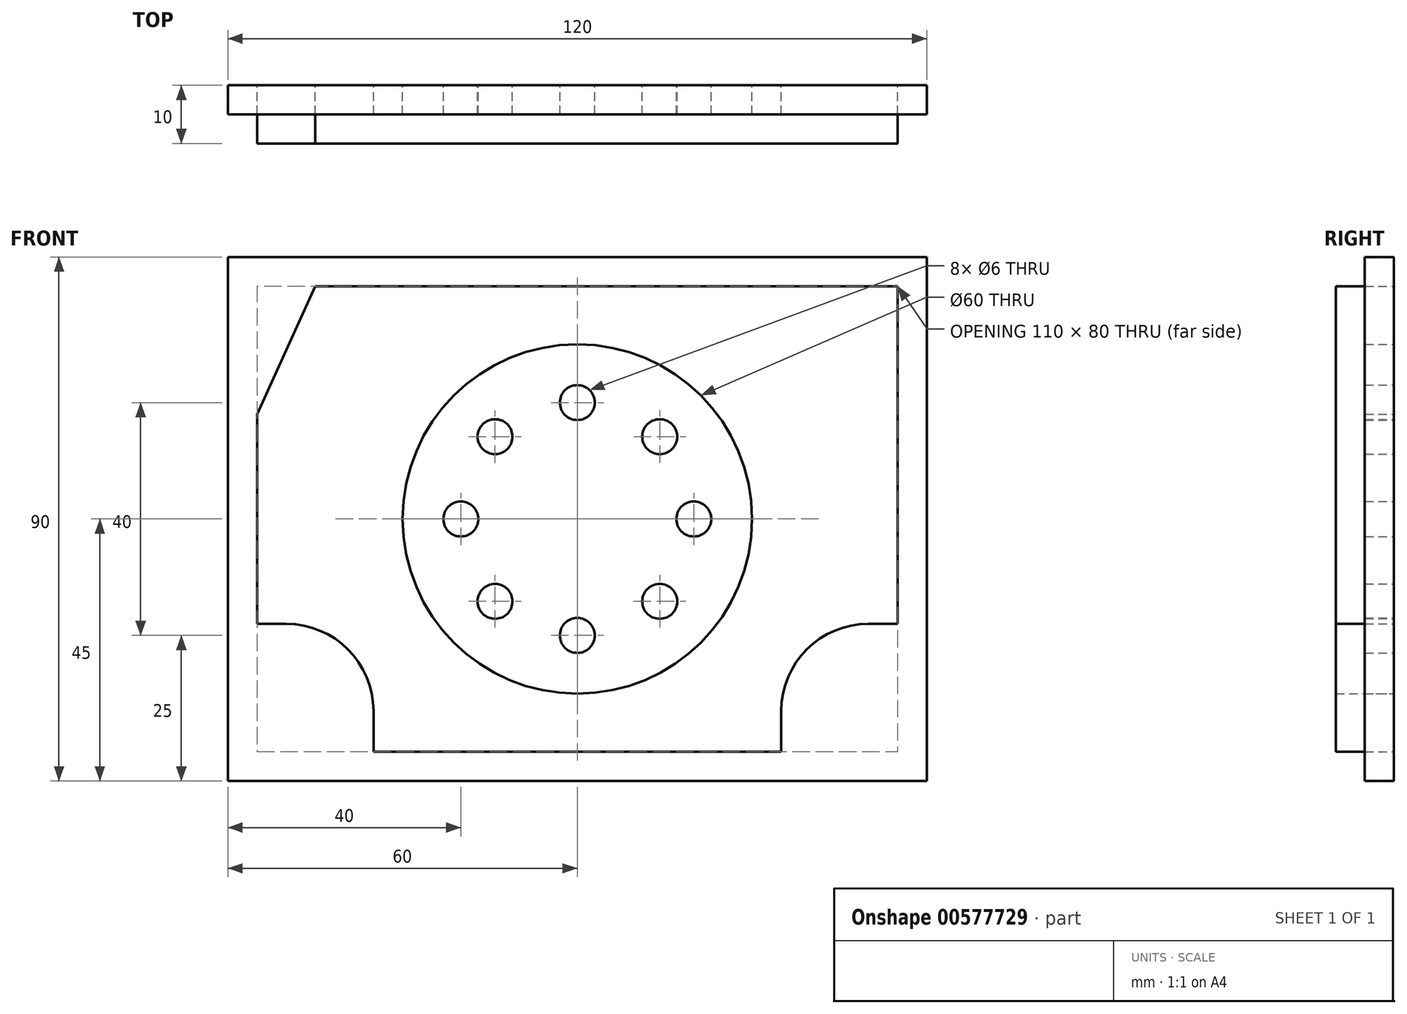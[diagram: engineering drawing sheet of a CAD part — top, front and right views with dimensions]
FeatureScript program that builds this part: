
annotation { "Feature Type Name" : "Feature", "Feature Type Description" : "" }
export const myFeature = defineFeature(function(context is Context, id is Id, definition is map)
    precondition{}
    {
        {
            var Q0;
            Q0=qCreatedBy(makeId("Front.planeOp"),FACE);
            var sketch = newSketch(context, id + "F0", { "sketchPlane" : qUnion([Q0])});
            skLineSegment(sketch, "E0", {"start": v(0, 0) * mm, "end": v(-120, 0) * mm});
            skLineSegment(sketch, "E1", {"start": v(-120, 0) * mm, "end": v(-120, 90) * mm});
            skLineSegment(sketch, "E2", {"start": v(-120, 90) * mm, "end": v(0, 90) * mm});
            skLineSegment(sketch, "E3", {"start": v(0, 90) * mm, "end": v(0, 0) * mm});
            skLineSegment(sketch, "E4", {"start": v(-115, 27) * mm, "end": v(-115, 63) * mm});
            skLineSegment(sketch, "E5", {"start": v(-115, 63) * mm, "end": v(-105, 85) * mm});
            skLineSegment(sketch, "E6", {"start": v(-105, 85) * mm, "end": v(-5, 85) * mm});
            skLineSegment(sketch, "E7", {"start": v(-5, 85) * mm, "end": v(-5, 27) * mm});
            skLineSegment(sketch, "E8", {"start": v(-25, 5) * mm, "end": v(-95, 5) * mm});
            skLineSegment(sketch, "E9", {"start": v(-95, 5) * mm, "end": v(-95, 12) * mm});
            skLineSegment(sketch, "E10", {"start": v(-115, 27) * mm, "end": v(-110, 27) * mm});
            skLineSegment(sketch, "E11", {"start": v(-25, 5) * mm, "end": v(-25, 12) * mm});
            skLineSegment(sketch, "E12", {"start": v(-5, 27) * mm, "end": v(-10, 27) * mm});
            skArc(sketch, "E13", {"start": v(-95, 12) * mm, "mid": v(-99.4, 22.6) * mm, "end": v(-110, 27) * mm});
            skArc(sketch, "E14", {"start": v(-10, 27) * mm, "mid": v(-20.6, 22.6) * mm, "end": v(-25, 12) * mm});
            skCircle(sketch, "E15", {"center": v(-60, 45) * mm, "radius": 30 * mm});
            skCircle(sketch, "E16", {"center": v(-60, 45) * mm, "radius": 20 * mm, "construction": true});
            skLineSegment(sketch, "E17", {"start": v(-60, 45) * mm, "end": v(-80, 45) * mm, "construction": true});
            skLineSegment(sketch, "E18", {"start": v(-60, 45) * mm, "end": v(-40, 45) * mm, "construction": true});
            skLineSegment(sketch, "E19", {"start": v(-60, 45) * mm, "end": v(-60, 65) * mm, "construction": true});
            skLineSegment(sketch, "E20", {"start": v(-60, 45) * mm, "end": v(-60, 25) * mm, "construction": true});
            skCircle(sketch, "E21", {"center": v(-40, 45) * mm, "radius": 3 * mm});
            skCircle(sketch, "E22", {"center": v(-60, 65) * mm, "radius": 3 * mm});
            skCircle(sketch, "E23", {"center": v(-80, 45) * mm, "radius": 3 * mm});
            skCircle(sketch, "E24", {"center": v(-60, 25) * mm, "radius": 3 * mm});
            skLineSegment(sketch, "E25", {"start": v(-60, 45) * mm, "end": v(-74.14, 30.86) * mm, "construction": true});
            skLineSegment(sketch, "E26", {"start": v(-60, 45) * mm, "end": v(-45.86, 59.14) * mm, "construction": true});
            skLineSegment(sketch, "E27", {"start": v(-60, 45) * mm, "end": v(-45.86, 30.86) * mm, "construction": true});
            skLineSegment(sketch, "E28", {"start": v(-60, 45) * mm, "end": v(-74.14, 59.14) * mm, "construction": true});
            skCircle(sketch, "E29", {"center": v(-74.14, 59.14) * mm, "radius": 3 * mm});
            skCircle(sketch, "E30", {"center": v(-45.86, 59.14) * mm, "radius": 3 * mm});
            skCircle(sketch, "E31", {"center": v(-45.86, 30.86) * mm, "radius": 3 * mm});
            skCircle(sketch, "E32", {"center": v(-74.14, 30.86) * mm, "radius": 3 * mm});
            skSolve(sketch);
        }
        {
            var Q0;
            Q0=makeQuery(id+"F0.imprint","IMPRINT",FACE,{"disambiguationData":[TD([[makeQuery(id+"F0.imprint","IMPRINT",EDGE,{"derivedFrom":sQuery(id+"F0.wireOp",EDGE,"E0")}),-1.0]])]});
            var Q1;
            Q1=makeQuery(id+"F0.imprint","IMPRINT",FACE,{"disambiguationData":[TD([[makeQuery(id+"F0.imprint","IMPRINT",EDGE,{"derivedFrom":sQuery(id+"F0.wireOp",EDGE,"E15")}),1.0]])]});
            extrude(context, id + "F1", {"entities" : qUnion([Q0, Q1]), "depth" : 5 * mm, "offsetDistance" : 25 * mm});
        }
        {
            var Q0;
            Q0=makeQuery(id+"F0.imprint","IMPRINT",FACE,{"disambiguationData":[TD([[makeQuery(id+"F0.imprint","IMPRINT",EDGE,{"derivedFrom":sQuery(id+"F0.wireOp",EDGE,"E4")}),-1.0]])]});
            extrude(context, id + "F2", {"entities" : qUnion([Q0]), "depth" : 10 * mm, "offsetDistance" : 25 * mm});
        }
    });
